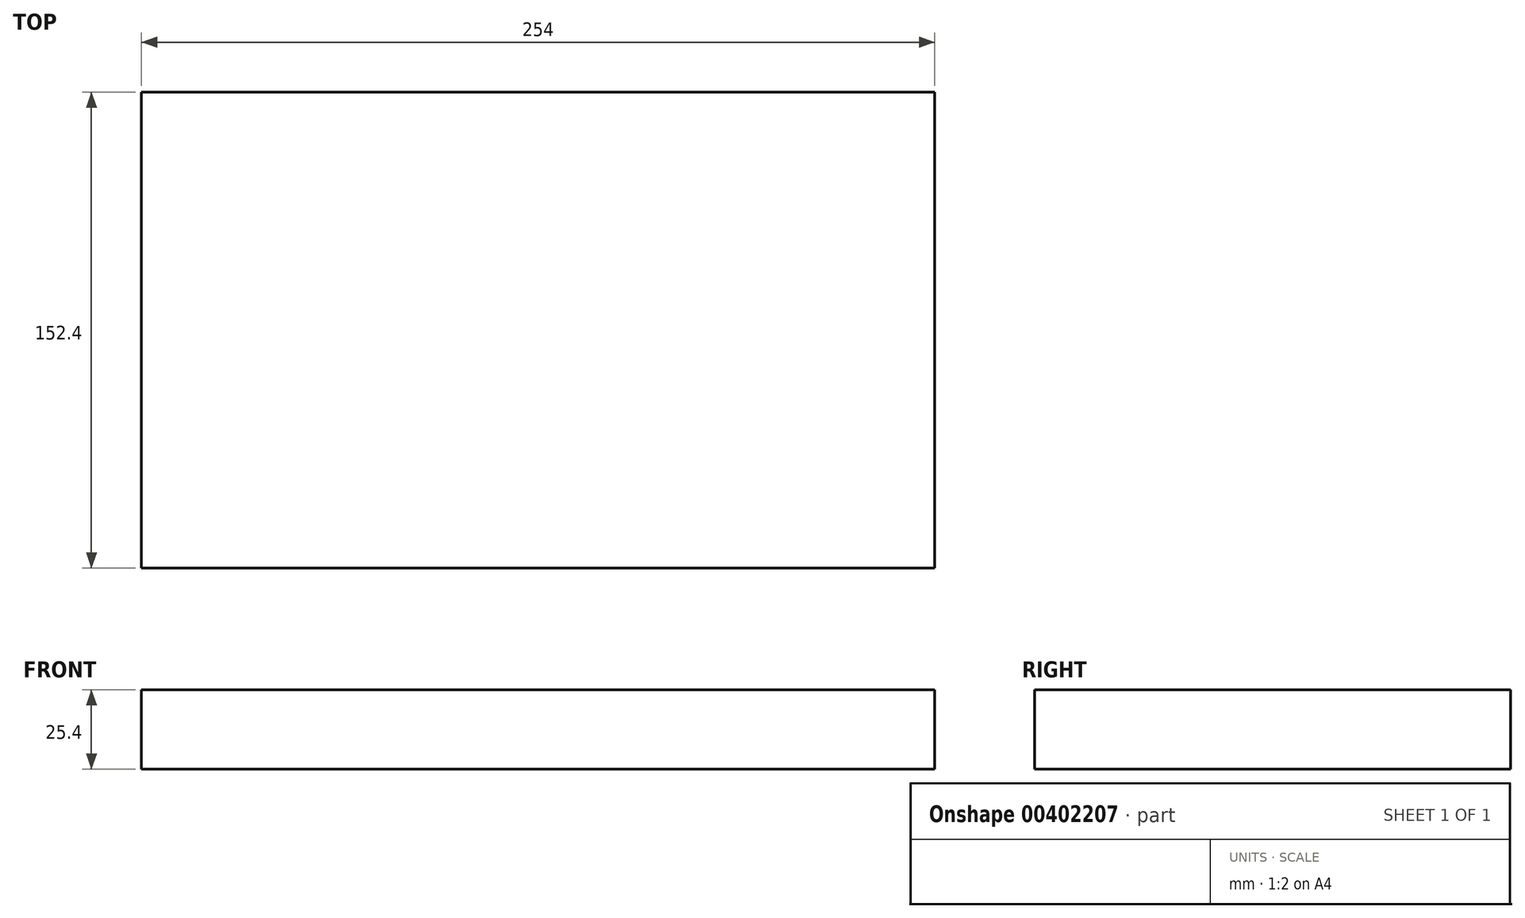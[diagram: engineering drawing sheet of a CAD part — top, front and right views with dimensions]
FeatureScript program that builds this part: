
annotation { "Feature Type Name" : "Feature", "Feature Type Description" : "" }
export const myFeature = defineFeature(function(context is Context, id is Id, definition is map)
    precondition{}
    {
        {
            var Q0;
            Q0=qCreatedBy(makeId("Top.planeOp"),FACE);
            var sketch = newSketch(context, id + "F0", { "sketchPlane" : qUnion([Q0])});
            skLineSegment(sketch, "E0.bottom", {"start": v(-127, 76.2) * mm, "end": v(127, 76.2) * mm});
            skLineSegment(sketch, "E0.top", {"start": v(-127, -76.2) * mm, "end": v(127, -76.2) * mm});
            skLineSegment(sketch, "E0.left", {"start": v(-127, 76.2) * mm, "end": v(-127, -76.2) * mm});
            skLineSegment(sketch, "E0.right", {"start": v(127, 76.2) * mm, "end": v(127, -76.2) * mm});
            skPoint(sketch, "E0.middle", {"position": v(0, 0) * mm});
            skSolve(sketch);
        }
        {
            var Q0;
            Q0 = qSketchRegion(id + "F0", true);
            extrude(context, id + "F1", {"entities" : qUnion([Q0]), "depth" : 25.4 * mm});
        }
    });
